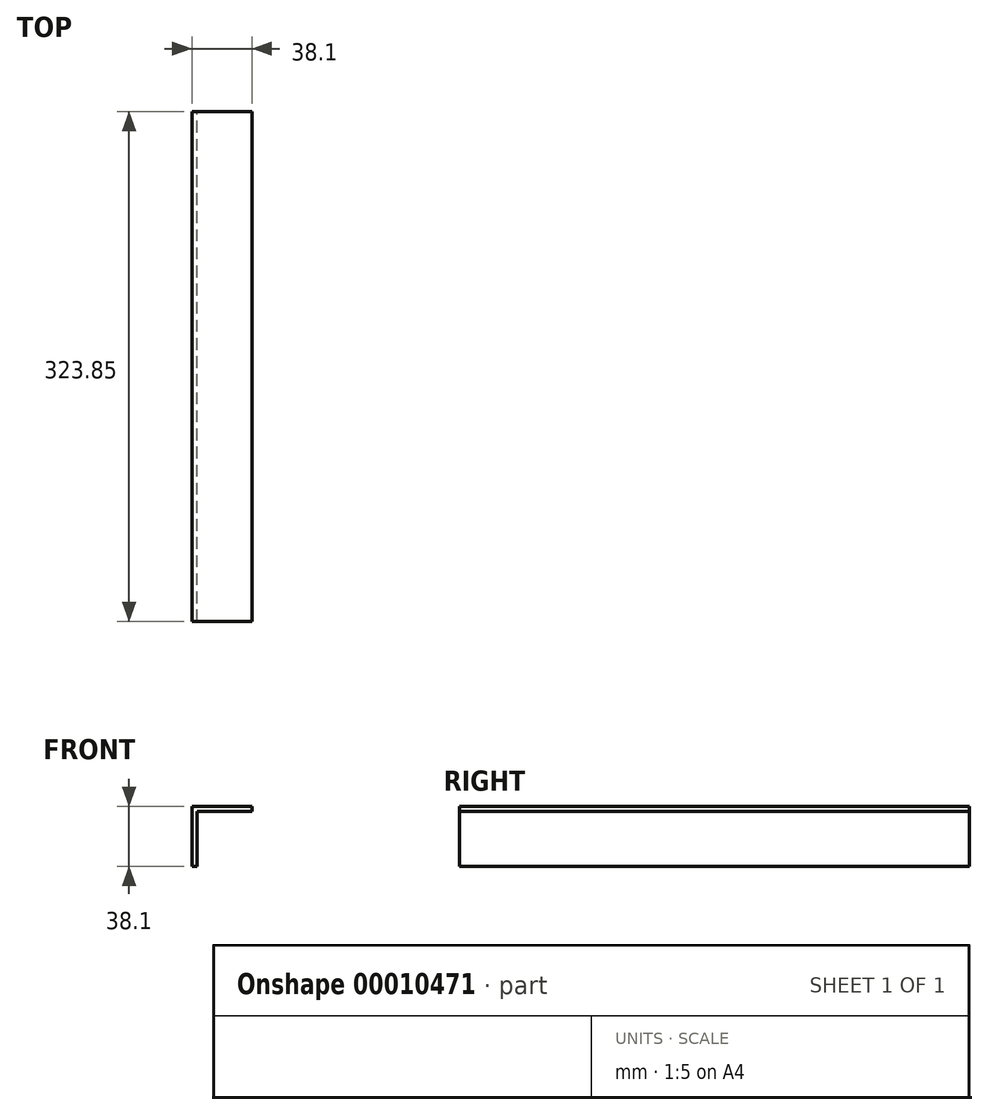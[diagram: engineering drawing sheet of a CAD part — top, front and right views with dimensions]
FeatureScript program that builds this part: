
annotation { "Feature Type Name" : "Feature", "Feature Type Description" : "" }
export const myFeature = defineFeature(function(context is Context, id is Id, definition is map)
    precondition{}
    {
        {
            var Q0;
            Q0=qCreatedBy(makeId("Front.planeOp"),FACE);
            var sketch = newSketch(context, id + "F0", { "sketchPlane" : qUnion([Q0])});
            skLineSegment(sketch, "E0", {"start": v(0, 0) * mm, "end": v(0, -34.93) * mm});
            skLineSegment(sketch, "E1", {"start": v(0, 0) * mm, "end": v(34.92, 0) * mm});
            skLineSegment(sketch, "E2.0", {"start": v(-3.18, 3.17) * mm, "end": v(-3.17, -34.93) * mm});
            skLineSegment(sketch, "E2.1", {"start": v(-3.18, 3.18) * mm, "end": v(34.92, 3.18) * mm});
            skLineSegment(sketch, "E3", {"start": v(-3.17, -34.93) * mm, "end": v(0, -34.93) * mm});
            skLineSegment(sketch, "E4", {"start": v(34.92, 0) * mm, "end": v(34.92, 3.18) * mm});
            skSolve(sketch);
        }
        {
            var Q0;
            Q0=qSketchRegion(id+"F0",true);
            extrude(context, id + "F1", {"entities" : qUnion([Q0]), "depth" : 323.85 * mm});
        }
    });
